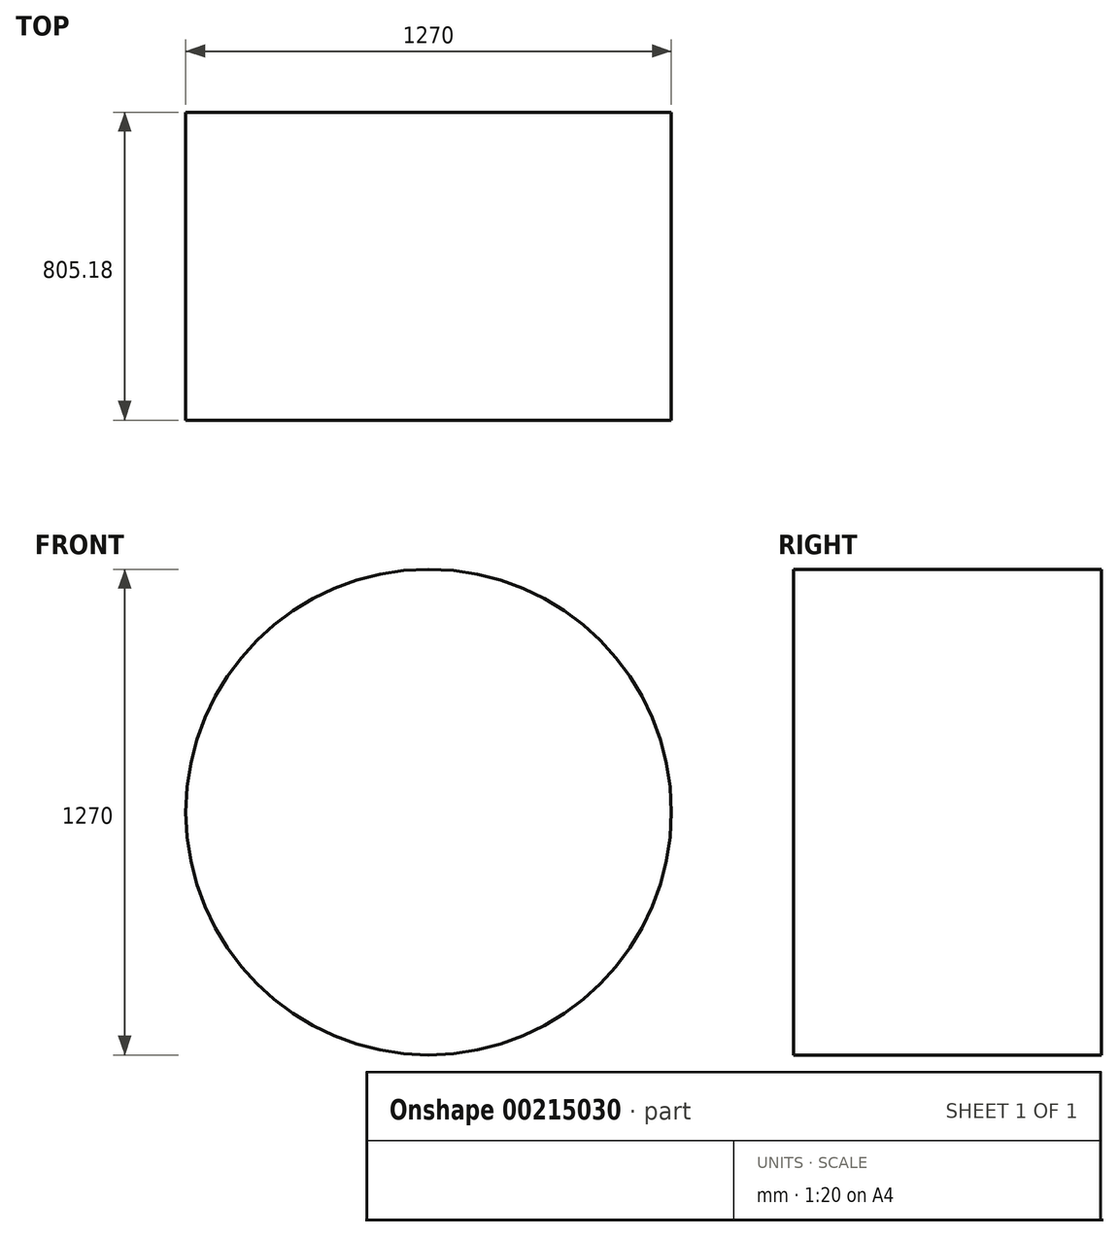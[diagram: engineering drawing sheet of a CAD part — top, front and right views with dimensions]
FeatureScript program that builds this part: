
annotation { "Feature Type Name" : "Feature", "Feature Type Description" : "" }
export const myFeature = defineFeature(function(context is Context, id is Id, definition is map)
    precondition{}
    {
        {
            var Q0;
            Q0=qCreatedBy(makeId("Front.planeOp"),FACE);
            var sketch = newSketch(context, id + "F0", { "sketchPlane" : qUnion([Q0])});
            skLineSegment(sketch, "E0.bottom", {"start": v(0, 0) * mm, "end": v(35.53, 0) * mm});
            skLineSegment(sketch, "E0.top", {"start": v(0, 19.93) * mm, "end": v(35.53, 19.93) * mm});
            skLineSegment(sketch, "E0.left", {"start": v(0, 0) * mm, "end": v(0, 19.93) * mm});
            skLineSegment(sketch, "E0.right", {"start": v(35.53, 0) * mm, "end": v(35.53, 19.93) * mm});
            skLineSegment(sketch, "E1.bottom", {"start": v(-29.63, -9.54) * mm, "end": v(17.22, -9.54) * mm});
            skLineSegment(sketch, "E1.top", {"start": v(-29.63, -20.4) * mm, "end": v(17.22, -20.4) * mm});
            skLineSegment(sketch, "E1.left", {"start": v(-29.63, -9.54) * mm, "end": v(-29.63, -20.4) * mm});
            skLineSegment(sketch, "E1.right", {"start": v(17.22, -9.54) * mm, "end": v(17.22, -20.4) * mm});
            skLineSegment(sketch, "E2", {"start": v(0, 19.93) * mm, "end": v(-29.63, -9.54) * mm});
            skLineSegment(sketch, "E3", {"start": v(17.22, -9.54) * mm, "end": v(35.53, 0) * mm});
            skCircle(sketch, "E4", {"center": v(0, 0) * mm, "radius": 38.1 * mm});
            skCircle(sketch, "E5", {"center": v(37.3, 7.75) * mm, "radius": 5.3 * mm});
            skSolve(sketch);
        }
        {
            var Q0;
            Q0=makeQuery(id+"F0.imprint","IMPRINT",FACE,{"disambiguationData":[TD([[makeQuery(id+"F0.imprint","IMPRINT",EDGE,{"derivedFrom":sQuery(id+"F0.wireOp",EDGE,"E0.bottom")}),1.0]])]});
            var Q1;
            Q1=makeQuery(id+"F0.imprint","IMPRINT",FACE,{"disambiguationData":[TD([[makeQuery(id+"F0.imprint","IMPRINT",EDGE,{"derivedFrom":sQuery(id+"F0.wireOp",EDGE,"E1.bottom")}),-1.0]])]});
            var Q2;
            Q2=makeQuery(id+"F0.imprint","IMPRINT",FACE,{"disambiguationData":[TD([[makeQuery(id+"F0.imprint","IMPRINT",EDGE,{"derivedFrom":sQuery(id+"F0.wireOp",EDGE,"E0.bottom")}),-1.0]])]});
            extrude(context, id + "F1", {"entities" : qUnion([Q0, Q1, Q2]), "depth" : 68.33 * mm});
        }
        {
            var Q0;
            Q0 = qSketchRegion(id + "F0", true);
            extrude(context, id + "F2", {"entities" : qUnion([Q0]), "operationType" : NewBodyOperationType.ADD, "depth" : 25.4 * mm});
        }
        {
            var Q0;
            Q0=makeQuery(id+"F1.opExtrude","SWEPT_BODY",BODY,{"disambiguationData":[OSD([sQuery(id+"F0.wireOp",EDGE,"E0.top"),sQuery(id+"F0.wireOp",EDGE,"E0.right"),sQuery(id+"F0.wireOp",EDGE,"E1.top"),sQuery(id+"F0.wireOp",EDGE,"E1.left"),sQuery(id+"F0.wireOp",EDGE,"E1.right"),sQuery(id+"F0.wireOp",EDGE,"E2"),sQuery(id+"F0.wireOp",EDGE,"E3"),sQuery(id+"F0.wireOp",EDGE,"E4"),sQuery(id+"F0.wireOp",EDGE,"E5")])]});
            deleteBodies(context, id + "F3", {"entities" : qUnion([Q0])});
        }
        {
            var Q0;
            Q0=qCreatedBy(makeId("Front.planeOp"),FACE);
            var sketch = newSketch(context, id + "F4", { "sketchPlane" : qUnion([Q0])});
            skCircle(sketch, "E6", {"center": v(0, 0) * mm, "radius": 635 * mm});
            skSolve(sketch);
        }
        {
            var Q0;
            Q0=makeQuery(id+"F4.imprint","IMPRINT",FACE,{"disambiguationData":[TD([[makeQuery(id+"F4.imprint","IMPRINT",EDGE,{"derivedFrom":sQuery(id+"F4.wireOp",EDGE,"E6")}),1.0]])]});
            extrude(context, id + "F5", {"entities" : qUnion([Q0]), "depth" : 805.18 * mm});
        }
    });
